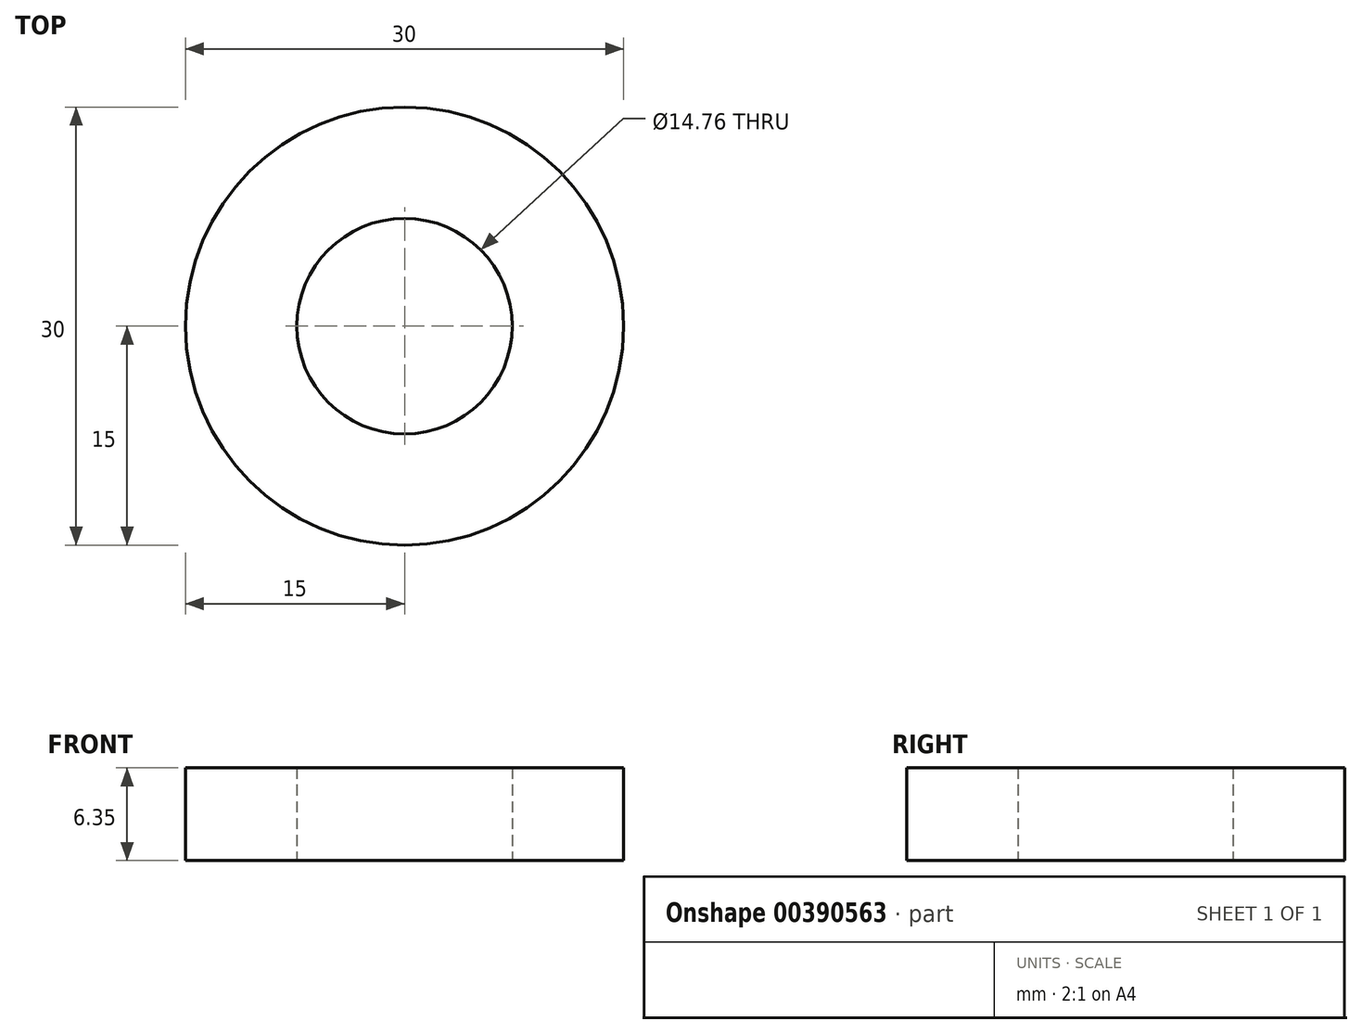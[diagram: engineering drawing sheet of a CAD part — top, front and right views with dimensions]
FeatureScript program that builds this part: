
annotation { "Feature Type Name" : "Feature", "Feature Type Description" : "" }
export const myFeature = defineFeature(function(context is Context, id is Id, definition is map)
    precondition{}
    {
        {
            var Q0;
            Q0=qCreatedBy(makeId("Top.planeOp"),FACE);
            var sketch = newSketch(context, id + "F0", { "sketchPlane" : qUnion([Q0])});
            skCircle(sketch, "E0", {"center": v(0, 0) * mm, "radius": 15 * mm});
            skCircle(sketch, "E1.0", {"center": v(0, 0) * mm, "radius": 7.38 * mm});
            skSolve(sketch);
        }
        {
            var Q0;
            Q0=makeQuery(id+"F0.imprint","IMPRINT",FACE,{"disambiguationData":[TD([[makeQuery(id+"F0.imprint","IMPRINT",EDGE,{"derivedFrom":sQuery(id+"F0.wireOp",EDGE,"E0")}),1.0]])]});
            extrude(context, id + "F1", {"entities" : qUnion([Q0]), "depth" : 6.35 * mm});
        }
    });
